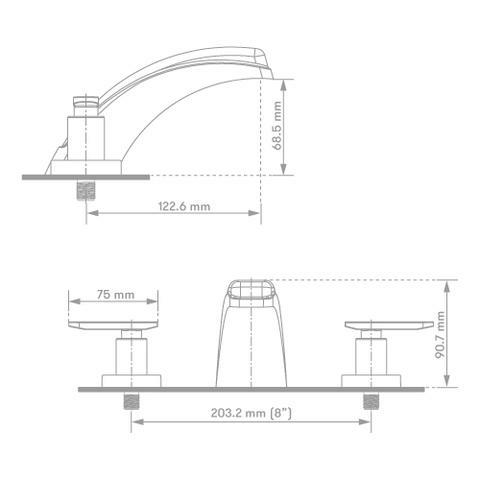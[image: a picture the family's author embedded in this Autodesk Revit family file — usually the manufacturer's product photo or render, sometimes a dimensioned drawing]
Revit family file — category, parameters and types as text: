
# Revit family: 01-1303-11 MEZCLADOR LAVAMANOS PLÁSTICO 8” ATLANTICO
name_source: partatom
category: Plumbing Fixtures
revit_build: Autodesk Revit 2018 (Build: 20170223_1515(x64)
units: mm (PartAtom-declared; Revit-internal decimal feet)

## family parameters
Cut with Voids When Loaded = No
Host = Face
OmniClass Number = 23.31.11.00
Part Type = Normal
Room Calculation Point = No
Round Connector Dimension = Use Diameter
Shared = No

## types (1)
- 01-1303-11
    Alto = 90 mm
    Alto - Aireador = 60 mm  [stored 0.19685 ft]
    Ancho manija = 66 mm
    CW Connection = Yes
    Default Elevation = 0 mm  [stored 0 ft]
    Description = Bimando baño
    Eje ( Rosca) = 203.2 mm  [stored 0.666667 ft]
    Eje-Aireador = 130 mm
    HW Connection = Yes
    Link Ficha Tecnica = http://infotecnica.gricol.com
    Manufacturer = Gricol
    Metal Laton Cromado = Metal Laton Cromado
    Model = 01-1303-11
    Plastico - ABS Cromado = Plastico - ABS Cromado
    Product Name = MEZCLADOR LAVAMANOS PLÁSTICO 8” ATLANTICO
    Type Image = MEZCLADOR LAVAMANOS PLÁSTICO 8” ATLANTICO.JPG
    URL = https://www.gricol.com
    Vent Connection = No
    Waste Connection = No

note: [stored X ft] marks values corroborated as IEEE doubles in the binary element streams (Revit-internal decimal feet)

## geometry (parser evidence)
native form markers: Blend x2, Sweep x3
no freeform markers — native parametric forms only
